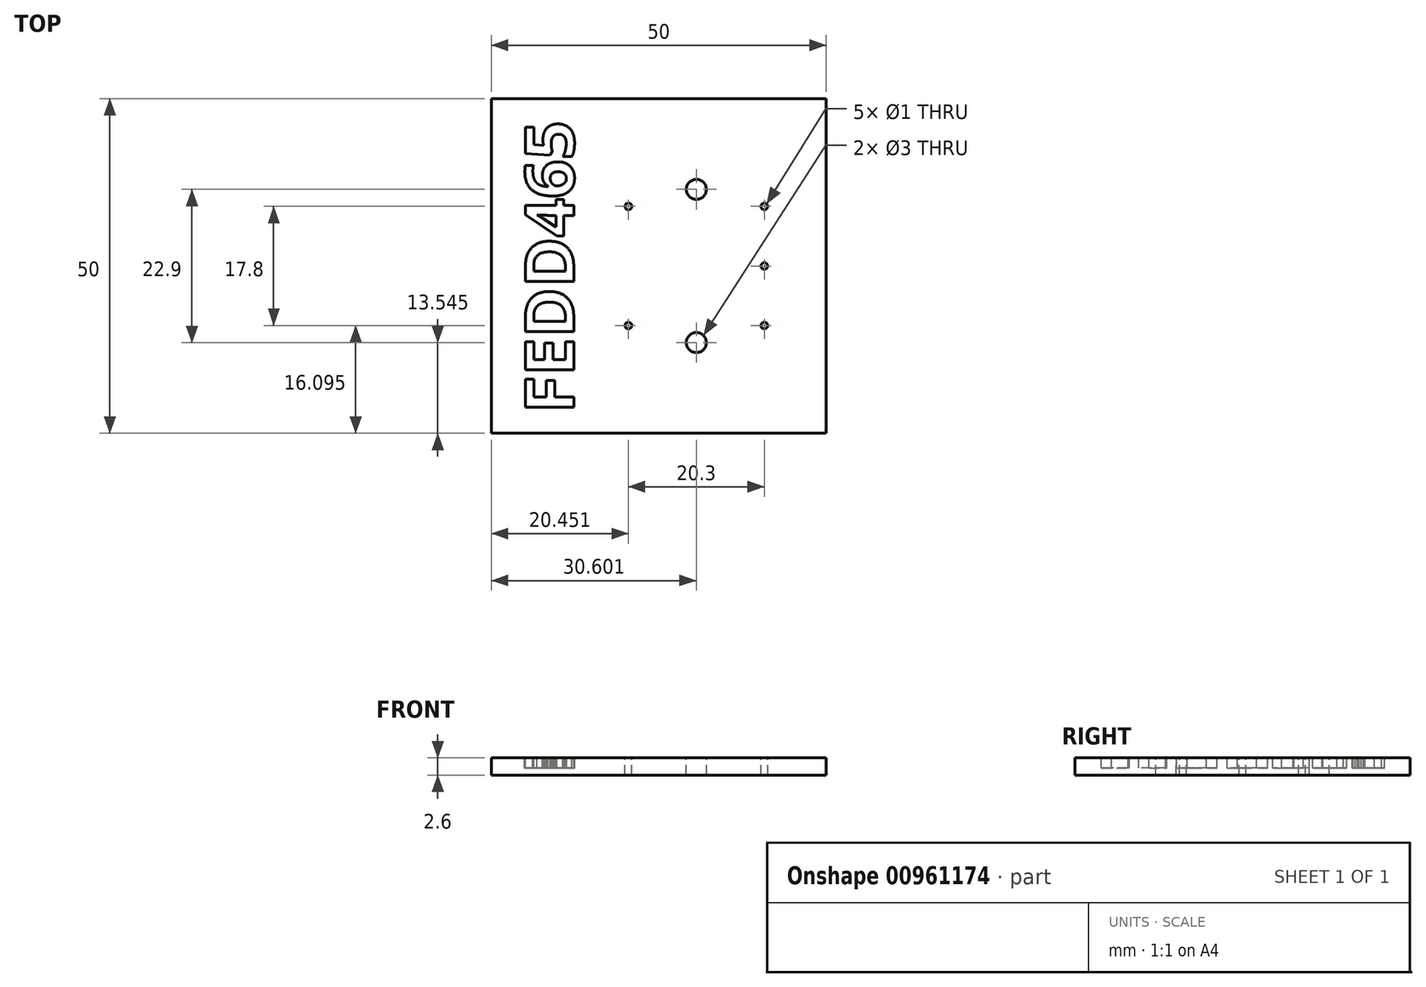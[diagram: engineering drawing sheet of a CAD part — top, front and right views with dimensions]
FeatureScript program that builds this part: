
annotation { "Feature Type Name" : "Feature", "Feature Type Description" : "" }
export const myFeature = defineFeature(function(context is Context, id is Id, definition is map)
    precondition{}
    {
        {
            var Q0;
            Q0=qCreatedBy(makeId("Top.planeOp"),FACE);
            var sketch = newSketch(context, id + "F0", { "sketchPlane" : qUnion([Q0])});
            skLineSegment(sketch, "E0.bottom", {"start": v(-43.16, 28.34) * mm, "end": v(6.84, 28.34) * mm});
            skLineSegment(sketch, "E0.top", {"start": v(-43.16, -21.66) * mm, "end": v(6.84, -21.66) * mm});
            skLineSegment(sketch, "E0.left", {"start": v(-43.16, 28.34) * mm, "end": v(-43.16, -21.66) * mm});
            skLineSegment(sketch, "E0.right", {"start": v(6.84, 28.34) * mm, "end": v(6.84, -21.66) * mm});
            skSolve(sketch);
        }
        {
            var Q0;
            Q0=makeQuery(id+"F0.imprint","IMPRINT",FACE,{"disambiguationData":[TD([[makeQuery(id+"F0.imprint","IMPRINT",EDGE,{"derivedFrom":sQuery(id+"F0.wireOp",EDGE,"E0.bottom")}),-1.0]])]});
            extrude(context, id + "F1", {"entities" : qUnion([Q0]), "depth" : 2.6 * mm, "offsetDistance" : 25 * mm});
        }
        {
            var Q0;
            Q0=makeQuery(id+"F1.opExtrude","CAP_FACE",FACE,{"disambiguationData":[OSD([sQuery(id+"F0.wireOp",EDGE,"E0.bottom"),sQuery(id+"F0.wireOp",EDGE,"E0.top"),sQuery(id+"F0.wireOp",EDGE,"E0.left"),sQuery(id+"F0.wireOp",EDGE,"E0.right")])],"isStart":false});
            var sketch = newSketch(context, id + "F2", { "sketchPlane" : qUnion([Q0])});
            skText(sketch, "E1", { "text": "FEDD465", "fontName": "OpenSans-Bold.ttf"});
            const initialGuessF2  = {"E1": [-0.03084, -0.01866, 0, 1, 0.00731]};
            skSetInitialGuess(sketch, initialGuessF2);
            skSolve(sketch);
        }
        {
            var Q0;
            Q0=qSketchRegion(id+"F2",true);
            extrude(context, id + "F3", {"entities" : qUnion([Q0]), "operationType" : NewBodyOperationType.REMOVE, "oppositeDirection" : true, "depth" : 1.5 * mm, "offsetDistance" : 25 * mm});
        }
        {
            var Q0;
            {var subQ0=sQuery(id+"F0.wireOp",EDGE,"E0.left");var subQ1=sQuery(id+"F0.wireOp",EDGE,"E0.bottom");var subQ2=sQuery(id+"F0.wireOp",EDGE,"E0.right");var subQ3=sQuery(id+"F0.wireOp",EDGE,"E0.top");Q0=makeQuery(id+"F3.boolean.opBoolean","SPLIT",FACE,{"disambiguationData":[TD([makeQuery(id+"F1.opExtrude","SWEPT_FACE",FACE,{"disambiguationData":[OSD([subQ1])]})])],"derivedFrom":makeQuery(id+"F1.opExtrude","CAP_FACE",FACE,{"disambiguationData":[OSD([subQ1,subQ3,subQ0,subQ2])],"isStart":false})});}
            var sketch = newSketch(context, id + "F4", { "sketchPlane" : qUnion([Q0])});
            skLineSegment(sketch, "E2.bottom", {"start": v(-26.16, -14.76) * mm, "end": v(1.04, -14.76) * mm});
            skLineSegment(sketch, "E2.top", {"start": v(-26.16, 21.44) * mm, "end": v(1.04, 21.44) * mm});
            skLineSegment(sketch, "E2.left", {"start": v(-26.16, -14.76) * mm, "end": v(-26.16, 21.44) * mm});
            skLineSegment(sketch, "E2.right", {"start": v(1.04, -14.76) * mm, "end": v(1.04, 21.44) * mm});
            skCircle(sketch, "E3", {"center": v(-22.7, -5.56) * mm, "radius": 0.5 * mm});
            skCircle(sketch, "E4", {"center": v(-22.7, 12.24) * mm, "radius": 0.5 * mm});
            skCircle(sketch, "E5", {"center": v(-12.56, 14.79) * mm, "radius": 1.5 * mm});
            skCircle(sketch, "E6", {"center": v(-2.4, 12.24) * mm, "radius": 0.5 * mm});
            skCircle(sketch, "E7", {"center": v(-2.4, 3.34) * mm, "radius": 0.5 * mm});
            skCircle(sketch, "E8", {"center": v(-2.4, -5.56) * mm, "radius": 0.5 * mm});
            skCircle(sketch, "E9", {"center": v(-12.56, -8.11) * mm, "radius": 1.5 * mm});
            skSolve(sketch);
        }
        {
            var Q0;
            Q0=makeQuery(id+"F4.imprint","IMPRINT",FACE,{"disambiguationData":[TD([[makeQuery(id+"F4.imprint","IMPRINT",EDGE,{"derivedFrom":sQuery(id+"F4.wireOp",EDGE,"E3")}),1.0]])]});
            var Q1;
            Q1=makeQuery(id+"F4.imprint","IMPRINT",FACE,{"disambiguationData":[TD([[makeQuery(id+"F4.imprint","IMPRINT",EDGE,{"derivedFrom":sQuery(id+"F4.wireOp",EDGE,"E5")}),1.0]])]});
            var Q2;
            Q2=makeQuery(id+"F4.imprint","IMPRINT",FACE,{"disambiguationData":[TD([[makeQuery(id+"F4.imprint","IMPRINT",EDGE,{"derivedFrom":sQuery(id+"F4.wireOp",EDGE,"E9")}),1.0]])]});
            var Q3;
            Q3=makeQuery(id+"F4.imprint","IMPRINT",FACE,{"disambiguationData":[TD([[makeQuery(id+"F4.imprint","IMPRINT",EDGE,{"derivedFrom":sQuery(id+"F4.wireOp",EDGE,"E4")}),1.0]])]});
            var Q4;
            Q4=makeQuery(id+"F4.imprint","IMPRINT",FACE,{"disambiguationData":[TD([[makeQuery(id+"F4.imprint","IMPRINT",EDGE,{"derivedFrom":sQuery(id+"F4.wireOp",EDGE,"E8")}),1.0]])]});
            var Q5;
            Q5=makeQuery(id+"F4.imprint","IMPRINT",FACE,{"disambiguationData":[TD([[makeQuery(id+"F4.imprint","IMPRINT",EDGE,{"derivedFrom":sQuery(id+"F4.wireOp",EDGE,"E7")}),1.0]])]});
            var Q6;
            Q6=makeQuery(id+"F4.imprint","IMPRINT",FACE,{"disambiguationData":[TD([[makeQuery(id+"F4.imprint","IMPRINT",EDGE,{"derivedFrom":sQuery(id+"F4.wireOp",EDGE,"E6")}),1.0]])]});
            extrude(context, id + "F5", {"entities" : qUnion([Q0, Q1, Q2, Q3, Q4, Q5, Q6]), "operationType" : NewBodyOperationType.REMOVE, "endBound" : BoundingType.UP_TO_NEXT, "oppositeDirection" : true, "depth" : 25 * mm, "offsetDistance" : 25 * mm});
        }
    });
